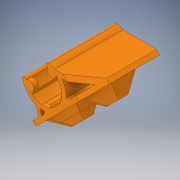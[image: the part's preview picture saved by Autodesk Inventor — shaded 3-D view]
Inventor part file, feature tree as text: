
AUTODESK INVENTOR PART (.ipt)
format: ipt  version: 2017 (Build 210142000, 142)  size: 1,051,136 bytes
history: native  units: in
note: dims shown in document units (in); Inventor stores cm internally (conversion verified against a paired STEP export)
features: extrude x3, sketch x3, other x2
ambient origin geometry x8: Origin, YZ Plane, XZ Plane, XY Plane, X Axis, Y Axis, Z Axis, Center Point
bodies: Solid1 (feature_tree)
feature tree (8):
  other  "10_Support plateau.STEP"
  extrude  "Extrusion1"  TaperAngle=0.0deg  [1 undecoded]
  extrude  "Extrusion3"  [1 undecoded]
  extrude  "Extrusion4"  [1 undecoded]
  sketch  "Sketch1"  dims[d0=0.3937in d1=0.0in d4=0.0in d5=0.0in]
  sketch  "Sketch3"  dims[d6=0.0in d7=0.0in]
  sketch  "Sketch4"
  parser-record x1  (decoder bookkeeping rows leaked as tree rows — omitted from the tree; the rows remain in map.json)
note: 3 required parameter values undecoded (feature->parameter linkage not recoverable at this tier; creation-order binding heuristic only, values carry confidence <= 0.55)
